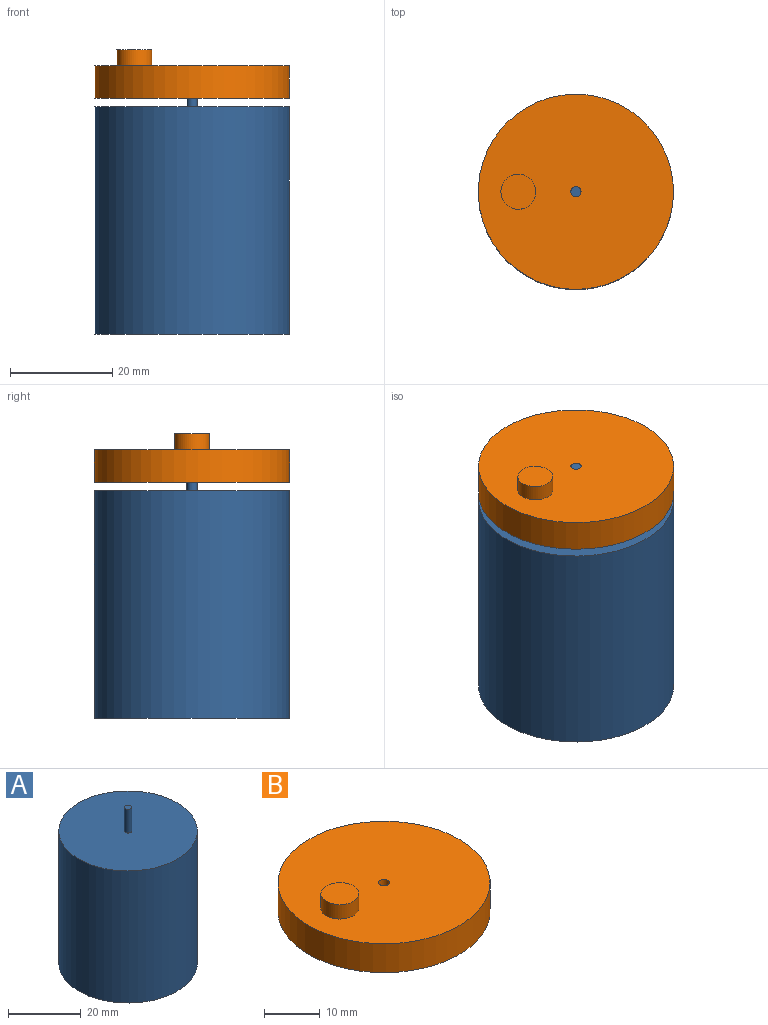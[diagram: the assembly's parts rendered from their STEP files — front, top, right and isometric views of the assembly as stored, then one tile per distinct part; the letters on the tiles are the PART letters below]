
ASSEMBLY  parts=2 mates=1
PART A: 5 faces, bbox 38.1x38.1x52.5 mm
  f0: cylinder r=19.05mm len=44.45mm, axis (0,0,-1), area 5320.4mm2, adj f1,f2
  f1: plane 38.1x38.1mm, normal (0,0,1), area 1137mm2, adj f0,f3
  f2: plane 38.1x38.1mm, normal (0,0,-1), area 1140.1mm2, adj f0
  f3: cylinder r=1mm len=8mm, axis (0,0,-1), area 50.3mm2, adj f1,f4
  f4: plane 2x2mm, normal (0,0,1), area 3.1mm2, adj f3
PART B: 6 faces, bbox 38.1x38.1x9.5 mm
  f0: cylinder r=1mm len=6.35mm, axis (0,0,-1), area 39.9mm2, adj f2,f3
  f1: cylinder r=19.05mm len=38.1mm, axis (0,0,-1), area 760.1mm2, adj f2,f3
  f2: plane 38.1x38.1mm, normal (0,0,1), area 1100.4mm2, adj f0,f1,f4
  f3: plane 38.1x38.1mm, normal (0,0,-1), area 1137mm2, adj f0,f1
  f4: cylinder r=3.41mm len=6.82mm, axis (0,0,-1), area 68.1mm2, adj f2,f5
  f5: plane 6.82x6.82mm, normal (0,0,1), area 36.6mm2, adj f4
PLACE A t=(-33.74,-7.18,-4.69)mm
PLACE B t=(-33.74,-7.18,41.41)mm
MATE revolute B.f0 <-> A.f0  axis (0,0,1) through (-33.74,-7.18,47.76)mm
